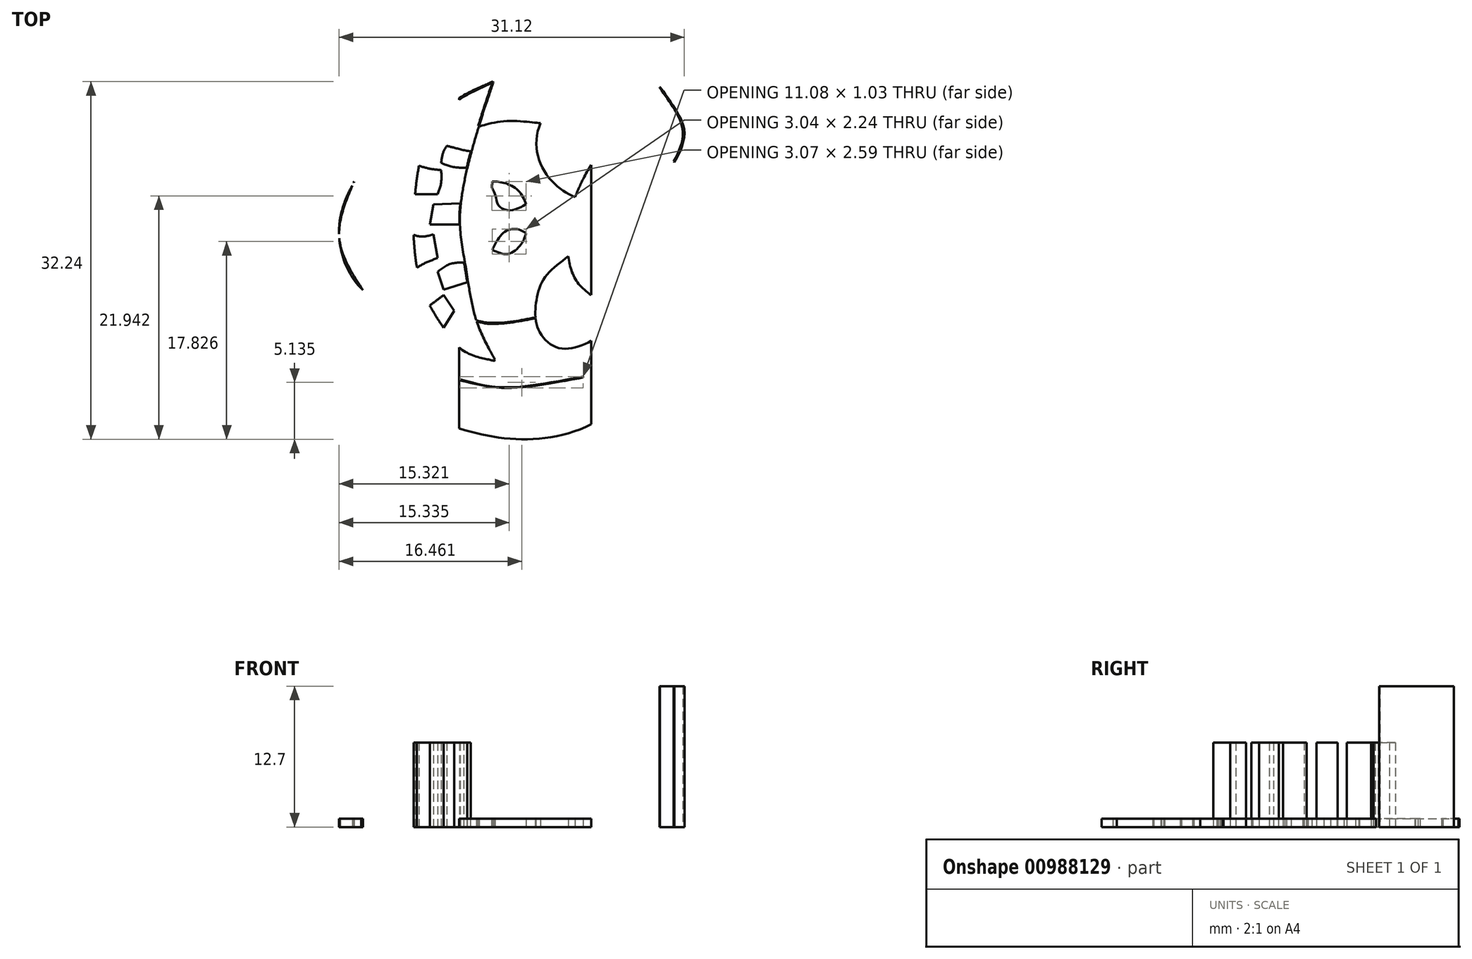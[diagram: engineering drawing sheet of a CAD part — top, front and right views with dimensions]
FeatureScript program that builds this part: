
annotation { "Feature Type Name" : "Feature", "Feature Type Description" : "" }
export const myFeature = defineFeature(function(context is Context, id is Id, definition is map)
    precondition{}
    {
        {
            var Q0;
            Q0=qCreatedBy(makeId("Top.planeOp"),FACE);
            var sketch = newSketch(context, id + "F0", { "sketchPlane" : qUnion([Q0])});
            skFitSpline(sketch, "E0", {"points": [v(-39.33, 53.9) * mm, v(-39.3, 55.65) * mm, v(-38.81, 56.88) * mm, v(-37.76, 58.43) * mm, v(-36.04, 59.76) * mm, v(-33.87, 60.77) * mm, v(-30.29, 61.56) * mm, v(-22.32, 61.02) * mm, v(-16.44, 57.51) * mm, v(-15.07, 52.72) * mm], "startDerivative": vector(-4.95, 22.44) * mm, "endDerivative": vector(4.37, -37.58) * mm});
            skFitSpline(sketch, "E1", {"points": [v(-15.07, 52.72) * mm, v(-13.86, 50.97) * mm, v(-12.98, 48.75) * mm, v(-13.85, 46.01) * mm], "startDerivative": vector(3.9, -5.4) * mm, "endDerivative": vector(-4.23, -7.42) * mm});
            skFitSpline(sketch, "E2", {"points": [v(-35.99, 54.58) * mm, v(-39.33, 53.9) * mm, v(-42.96, 50.45) * mm, v(-43.02, 47.15) * mm, v(-42.62, 44.27) * mm], "startDerivative": vector(-13.39, 1.37) * mm, "endDerivative": vector(3.7, -13.44) * mm});
            skFitSpline(sketch, "E3", {"points": [v(-39.96, 46.71) * mm, v(-42.62, 44.27) * mm, v(-43.95, 39.17) * mm, v(-41.83, 34.5) * mm, v(-38.06, 32.62) * mm], "startDerivative": vector(-12.7, -9.2) * mm, "endDerivative": vector(16.83, -5.57) * mm});
            skFitSpline(sketch, "E4", {"points": [v(-41.83, 34.5) * mm, v(-42.62, 32.56) * mm, v(-41.12, 28.84) * mm, v(-37.17, 25.72) * mm], "startDerivative": vector(-4.3, -6.86) * mm, "endDerivative": vector(11.03, -7.12) * mm});
            skFitSpline(sketch, "E5", {"points": [v(-38.62, 26.65) * mm, v(-38.4, 24.69) * mm, v(-33.93, 22.27) * mm, v(-27.64, 21.04) * mm, v(-21.05, 22.48) * mm, v(-16.17, 26.13) * mm, v(-15.07, 27.44) * mm, v(-14.53, 30.03) * mm], "startDerivative": vector(-3.87, -20.06) * mm, "endDerivative": vector(-7.64, 24.65) * mm});
            skFitSpline(sketch, "E6", {"points": [v(-19.88, 54.85) * mm, v(-17.7, 54.2) * mm, v(-15.07, 52.72) * mm], "startDerivative": vector(4.65, -1.07) * mm, "endDerivative": vector(4.98, -3.14) * mm});
            skFitSpline(sketch, "E7", {"points": [v(-33.22, 54.9) * mm, v(-27.82, 55.84) * mm, v(-22.66, 55.1) * mm], "startDerivative": vector(10.73, 2.71) * mm, "endDerivative": vector(10.4, -2.34) * mm});
            skFitSpline(sketch, "E8", {"points": [v(-16.1, 47.7) * mm, v(-13.85, 46.01) * mm, v(-12.23, 40.7) * mm, v(-14.4, 36.61) * mm, v(-16.63, 34.68) * mm], "startDerivative": vector(12.14, -5.68) * mm, "endDerivative": vector(-9.97, -7.78) * mm});
            skFitSpline(sketch, "E9", {"points": [v(-19.55, 27.44) * mm, v(-16.08, 29.12) * mm, v(-14.53, 30.03) * mm, v(-13, 33.5) * mm, v(-13.94, 37.12) * mm], "startDerivative": vector(14.06, 7.1) * mm, "endDerivative": vector(-7.18, 12.36) * mm});
            skFitSpline(sketch, "E10", {"points": [v(-13.54, 36.36) * mm, v(-12.33, 36.37) * mm, v(-8.7, 39.02) * mm, v(-7.42, 41.88) * mm, v(-7.4, 45.45) * mm, v(-8.5, 47.8) * mm, v(-9.45, 49.69) * mm, v(-9.37, 51.2) * mm, v(-9.03, 51.67) * mm, v(-8.36, 51.6) * mm, v(-8.53, 52.66) * mm, v(-9.37, 53.43) * mm, v(-10.12, 53.75) * mm, v(-10.81, 53.13) * mm, v(-11.23, 51.87) * mm, v(-10.59, 49.69) * mm, v(-10.5, 47.55) * mm, v(-11.68, 44.98) * mm, v(-12.4, 44.5) * mm, v(-13.1, 44.77) * mm], "startDerivative": vector(23.37, -4.73) * mm, "endDerivative": vector(-22.8, 5.66) * mm});
            skFitSpline(sketch, "E11", {"points": [v(-33.05, 26.34) * mm, v(-30.37, 25.77) * mm, v(-27.8, 25.7) * mm, v(-24.12, 26.22) * mm, v(-21.97, 26.62) * mm], "startDerivative": vector(11, -2.7) * mm, "endDerivative": vector(8.86, 1.67) * mm});
            skFitSpline(sketch, "E12", {"points": [v(-18.47, 48.14) * mm, v(-19.94, 49.85) * mm, v(-22.3, 51.1) * mm, v(-24.87, 50.74) * mm, v(-26.13, 48.44) * mm, v(-25.8, 45.87) * mm, v(-24.3, 43.84) * mm, v(-22.71, 42.87) * mm], "startDerivative": vector(-9.65, 13) * mm, "endDerivative": vector(12.95, -6.46) * mm});
            skFitSpline(sketch, "E13", {"points": [v(-23.3, 37.54) * mm, v(-22.32, 34.98) * mm, v(-19.16, 33.05) * mm], "startDerivative": vector(0.74, -6.31) * mm, "endDerivative": vector(7.38, -2.76) * mm});
            skFitSpline(sketch, "E14", {"points": [v(-19.16, 33.05) * mm, v(-19.6, 31.41) * mm, v(-21.62, 29.72) * mm, v(-24.3, 29.31) * mm, v(-26.01, 30.94) * mm, v(-26.25, 33.05) * mm, v(-25.57, 35.4) * mm, v(-23.3, 37.54) * mm], "startDerivative": vector(-1.66, -13.93) * mm, "endDerivative": vector(16.3, 12.24) * mm});
            skFitSpline(sketch, "E15", {"points": [v(-30.15, 38.12) * mm, v(-28.76, 37.75) * mm, v(-27.56, 38.62) * mm, v(-27.11, 39.62) * mm], "startDerivative": vector(4.14, -1.94) * mm, "endDerivative": vector(1.04, 3.31) * mm});
            skFitSpline(sketch, "E16", {"points": [v(-27.11, 39.62) * mm, v(-28, 40) * mm, v(-29.2, 39.62) * mm, v(-30.15, 38.12) * mm], "startDerivative": vector(-2.92, 1.76) * mm, "endDerivative": vector(-2.2, -4.45) * mm});
            skFitSpline(sketch, "E17", {"points": [v(-30.15, 44.28) * mm, v(-30.15, 43.62) * mm, v(-29.91, 43.16) * mm, v(-29.61, 42.14) * mm, v(-28.55, 41.68) * mm, v(-27.11, 42.23) * mm], "startDerivative": vector(-0.6, -4.34) * mm, "endDerivative": vector(5.6, 3.12) * mm});
            skFitSpline(sketch, "E18", {"points": [v(-27.11, 42.23) * mm, v(-27.8, 43.44) * mm, v(-29.14, 44.17) * mm, v(-30.15, 44.28) * mm], "startDerivative": vector(-1.53, 3.82) * mm, "endDerivative": vector(-3.36, 0.08) * mm});
            skFitSpline(sketch, "E19", {"points": [v(-30, 28.19) * mm, v(-31.65, 31.78) * mm, v(-32.6, 36.37) * mm, v(-33.12, 41.13) * mm, v(-32, 47.3) * mm, v(-30.15, 53.2) * mm], "startDerivative": vector(-10.57, 19.5) * mm, "endDerivative": vector(8.94, 26.24) * mm});
            skFitSpline(sketch, "E20", {"points": [v(-30.15, 53.2) * mm, v(-34.92, 50.14) * mm, v(-37.07, 43.64) * mm, v(-36.79, 35.77) * mm, v(-34.79, 31.44) * mm, v(-32.56, 29.09) * mm, v(-30, 28.19) * mm], "startDerivative": vector(-29.73, -13.8) * mm, "endDerivative": vector(21.62, -5.1) * mm});
            skFitSpline(sketch, "E21", {"points": [v(-32.1, 47) * mm, v(-33.52, 47.3) * mm, v(-34.27, 47.5) * mm], "startDerivative": vector(-2.65, 0.19) * mm, "endDerivative": vector(-1.62, 0.48) * mm});
            skFitSpline(sketch, "E22", {"points": [v(-34.27, 47.5) * mm, v(-34.57, 46.95) * mm, v(-34.77, 45.96) * mm], "startDerivative": vector(-0.75, -1.12) * mm, "endDerivative": vector(-0.27, -1.92) * mm});
            skFitSpline(sketch, "E23", {"points": [v(-34.77, 45.96) * mm, v(-34.04, 45.68) * mm, v(-33.1, 45.52) * mm, v(-32.47, 45.53) * mm], "startDerivative": vector(2.06, -0.9) * mm, "endDerivative": vector(1.93, 0.12) * mm});
            skFitSpline(sketch, "E24", {"points": [v(-36.77, 45.7) * mm, v(-35.85, 45.44) * mm, v(-34.77, 45.3) * mm], "startDerivative": vector(2.13, -0.61) * mm, "endDerivative": vector(2.17, -0.22) * mm});
            skFitSpline(sketch, "E25", {"points": [v(-34.77, 45.3) * mm, v(-34.77, 44.2) * mm, v(-35.1, 43.13) * mm], "startDerivative": vector(0.16, -2.22) * mm, "endDerivative": vector(-0.8, -2.13) * mm});
            skFitSpline(sketch, "E26", {"points": [v(-35.1, 43.13) * mm, v(-36.1, 43.13) * mm, v(-37.12, 43.13) * mm], "startDerivative": vector(-2.06, 0) * mm, "endDerivative": vector(-2.4, 0) * mm});
            skFitSpline(sketch, "E27", {"points": [v(-33.04, 42.3) * mm, v(-35.47, 42.22) * mm], "startDerivative": vector(-2.44, -0.09) * mm, "endDerivative": vector(-2.44, -0.09) * mm});
            skFitSpline(sketch, "E28", {"points": [v(-35.47, 42.22) * mm, v(-35.79, 40.39) * mm], "startDerivative": vector(-0.32, -1.83) * mm, "endDerivative": vector(-0.32, -1.83) * mm});
            skFitSpline(sketch, "E29", {"points": [v(-35.79, 40.39) * mm, v(-33.12, 40.39) * mm], "startDerivative": vector(2.63, 0) * mm, "endDerivative": vector(2.63, 0) * mm});
            skFitSpline(sketch, "E30", {"points": [v(-37.25, 39.46) * mm, v(-36.5, 39.3) * mm, v(-35.47, 39.5) * mm], "startDerivative": vector(2.1, -0.63) * mm, "endDerivative": vector(2.75, 0.75) * mm});
            skFitSpline(sketch, "E31", {"points": [v(-35.47, 39.5) * mm, v(-35.1, 37.37) * mm], "startDerivative": vector(0.38, -2.13) * mm, "endDerivative": vector(0.38, -2.13) * mm});
            skFitSpline(sketch, "E32", {"points": [v(-35.1, 37.37) * mm, v(-36.15, 36.96) * mm, v(-36.95, 36.51) * mm], "startDerivative": vector(-2.1, -0.75) * mm, "endDerivative": vector(-1.64, -0.98) * mm});
            skFitSpline(sketch, "E33", {"points": [v(-32.71, 37) * mm, v(-34.04, 36.82) * mm, v(-35.1, 36.13) * mm], "startDerivative": vector(-2.66, -0.07) * mm, "endDerivative": vector(-2.01, -1.63) * mm});
            skFitSpline(sketch, "E34", {"points": [v(-35.1, 36.13) * mm, v(-34.55, 34.52) * mm], "startDerivative": vector(0.54, -1.6) * mm, "endDerivative": vector(0.54, -1.6) * mm});
            skFitSpline(sketch, "E35", {"points": [v(-34.55, 34.52) * mm, v(-32.41, 35.2) * mm], "startDerivative": vector(2.1, 0.68) * mm, "endDerivative": vector(2.1, 0.68) * mm});
            skFitSpline(sketch, "E36", {"points": [v(-35.79, 33.1) * mm, v(-34.55, 34.04) * mm], "startDerivative": vector(1.24, 0.9) * mm, "endDerivative": vector(1.24, 0.9) * mm});
            skFitSpline(sketch, "E37", {"points": [v(-34.55, 34.04) * mm, v(-33.6, 32.62) * mm], "startDerivative": vector(0.95, -1.42) * mm, "endDerivative": vector(0.95, -1.42) * mm});
            skFitSpline(sketch, "E38", {"points": [v(-33.6, 32.62) * mm, v(-34.55, 31.1) * mm], "startDerivative": vector(-0.95, -1.52) * mm, "endDerivative": vector(-0.95, -1.52) * mm});
            skFitSpline(sketch, "E39", {"points": [v(-31.43, 49.3) * mm, v(-29, 49.76) * mm, v(-25.77, 49.61) * mm], "startDerivative": vector(5, 1.26) * mm, "endDerivative": vector(6.26, -0.6) * mm});
            skFitSpline(sketch, "E40", {"points": [v(-31.65, 31.78) * mm, v(-30.53, 31.55) * mm, v(-28.49, 31.64) * mm, v(-26.27, 32.02) * mm], "startDerivative": vector(3.97, -1.1) * mm, "endDerivative": vector(5.9, 1.12) * mm});
            skFitSpline(sketch, "E41", {"points": [v(-13.85, 46.01) * mm, v(-13.38, 45.62) * mm, v(-13.1, 44.77) * mm], "startDerivative": vector(0.96, -1.11) * mm, "endDerivative": vector(0.12, -1.6) * mm});
            skFitSpline(sketch, "E42", {"points": [v(-13.54, 36.36) * mm, v(-13, 33.5) * mm, v(-14.53, 30.03) * mm], "startDerivative": vector(2.2, -6) * mm, "endDerivative": vector(-6.3, -4.5) * mm});
            skFitSpline(sketch, "E43", {"points": [v(-18.47, 48.14) * mm, v(-20.62, 46.55) * mm, v(-22.2, 44.02) * mm, v(-22.71, 42.87) * mm], "startDerivative": vector(-6.1, -3.67) * mm, "endDerivative": vector(-1.87, -4.03) * mm});
            skFitSpline(sketch, "E44", {"points": [v(-42.62, 44.27) * mm, v(-43.95, 39.17) * mm, v(-41.83, 34.5) * mm], "startDerivative": vector(-4.46, -10.28) * mm, "endDerivative": vector(6, -9.2) * mm});
            skLineSegment(sketch, "E45.left", {"start": v(-21.23, 60.69) * mm, "end": v(-21.23, 50.72) * mm});
            skLineSegment(sketch, "E45.right", {"start": v(-33.16, 60.92) * mm, "end": v(-33.16, 51.65) * mm});
            skFitSpline(sketch, "E46.0", {"points": [v(-39.58, 26.84) * mm, v(-39.63, 26.61) * mm, v(-39.7, 26.11) * mm, v(-39.7, 25.38) * mm, v(-39.54, 24.75) * mm, v(-39.36, 24.36) * mm, v(-39.16, 24.06) * mm, v(-38.94, 23.79) * mm, v(-38.64, 23.48) * mm, v(-38.22, 23.15) * mm, v(-37.61, 22.75) * mm, v(-36.77, 22.31) * mm, v(-35.67, 21.85) * mm, v(-34.53, 21.43) * mm, v(-33.4, 21.06) * mm, v(-31.88, 20.63) * mm, v(-29.97, 20.22) * mm, v(-27.63, 20) * mm, v(-25.61, 20.1) * mm, v(-23.99, 20.38) * mm, v(-22.77, 20.7) * mm, v(-21.77, 21.06) * mm, v(-20.97, 21.42) * mm, v(-20.19, 21.82) * mm, v(-19.24, 22.38) * mm, v(-18.19, 23.12) * mm, v(-17.23, 23.88) * mm, v(-16.39, 24.6) * mm, v(-15.8, 25.13) * mm, v(-15.42, 25.49) * mm, v(-15.17, 25.73) * mm, v(-14.95, 25.97) * mm, v(-14.73, 26.2) * mm, v(-14.53, 26.47) * mm, v(-14.34, 26.74) * mm, v(-14.17, 27.04) * mm, v(-13.98, 27.38) * mm, v(-13.8, 27.77) * mm, v(-13.59, 28.35) * mm, v(-13.4, 29.18) * mm, v(-13.48, 29.94) * mm, v(-13.6, 30.32) * mm]});
            skFitSpline(sketch, "E47.0", {"points": [v(-42.9, 35.18) * mm, v(-43, 35.04) * mm, v(-43.19, 34.74) * mm, v(-43.5, 34.19) * mm, v(-43.72, 33.62) * mm, v(-43.84, 33.1) * mm, v(-43.9, 32.68) * mm, v(-43.9, 32.25) * mm, v(-43.84, 31.68) * mm, v(-43.7, 30.98) * mm, v(-43.4, 30.15) * mm, v(-43, 29.34) * mm, v(-42.51, 28.55) * mm, v(-41.94, 27.81) * mm, v(-41.3, 27.16) * mm, v(-40.42, 26.37) * mm, v(-39.25, 25.54) * mm, v(-38.32, 24.94) * mm, v(-37.86, 24.65) * mm]});
            skFitSpline(sketch, "E48.0", {"points": [v(-43.78, 44.77) * mm, v(-43.97, 44.34) * mm, v(-44.35, 43.46) * mm, v(-44.77, 42.31) * mm, v(-45.03, 41.36) * mm, v(-45.17, 40.63) * mm, v(-45.25, 39.87) * mm, v(-45.24, 39.23) * mm, v(-45.18, 38.71) * mm, v(-45.1, 38.21) * mm, v(-44.93, 37.6) * mm, v(-44.67, 36.9) * mm, v(-44.26, 36.02) * mm, v(-43.66, 34.98) * mm, v(-43.14, 34.2) * mm, v(-42.9, 33.81) * mm]});
            skFitSpline(sketch, "E49.0", {"points": [v(-35.86, 55.85) * mm, v(-36.54, 55.92) * mm, v(-37.93, 55.86) * mm, v(-39.67, 55.2) * mm, v(-41.1, 54.36) * mm, v(-42.12, 53.58) * mm, v(-42.9, 52.83) * mm, v(-43.45, 52.16) * mm, v(-43.8, 51.62) * mm, v(-44.06, 51.14) * mm, v(-44.22, 50.73) * mm, v(-44.34, 50.33) * mm, v(-44.44, 49.83) * mm, v(-44.5, 49.06) * mm, v(-44.47, 48.36) * mm, v(-44.39, 47.74) * mm, v(-44.34, 47.38) * mm, v(-44.3, 47.11) * mm, v(-44.27, 46.86) * mm, v(-44.24, 46.55) * mm, v(-44.2, 46.16) * mm, v(-44.15, 45.62) * mm, v(-44.06, 44.9) * mm, v(-43.93, 44.26) * mm, v(-43.84, 43.93) * mm]});
            skFitSpline(sketch, "E50.0", {"points": [v(-40.58, 53.62) * mm, v(-40.65, 53.95) * mm, v(-40.71, 54.6) * mm, v(-40.65, 55.49) * mm, v(-40.47, 56.28) * mm, v(-40.24, 56.86) * mm, v(-40.04, 57.29) * mm, v(-39.88, 57.6) * mm, v(-39.7, 57.92) * mm, v(-39.41, 58.37) * mm, v(-39.08, 58.84) * mm, v(-38.68, 59.3) * mm, v(-38.25, 59.75) * mm, v(-37.67, 60.23) * mm, v(-36.94, 60.72) * mm, v(-36.2, 61.14) * mm, v(-35.42, 61.52) * mm, v(-34.6, 61.86) * mm, v(-33.74, 62.16) * mm, v(-32.8, 62.43) * mm, v(-31.73, 62.65) * mm, v(-30.54, 62.82) * mm, v(-29.2, 62.93) * mm, v(-27.72, 62.96) * mm, v(-26.15, 62.9) * mm, v(-24.54, 62.75) * mm, v(-22.91, 62.48) * mm, v(-21.3, 62.08) * mm, v(-19.78, 61.53) * mm, v(-18.36, 60.84) * mm, v(-17.08, 60) * mm, v(-16.16, 59.18) * mm, v(-15.53, 58.43) * mm, v(-14.99, 57.63) * mm, v(-14.5, 56.58) * mm, v(-14.15, 55.3) * mm, v(-13.94, 54.06) * mm, v(-13.85, 53.26) * mm, v(-13.8, 52.86) * mm]});
            skFitSpline(sketch, "E51", {"points": [v(-13.8, 52.86) * mm, v(-13.4, 52.11) * mm, v(-12.4, 52.26) * mm, v(-11.8, 53.48) * mm, v(-10.42, 54.64) * mm, v(-7.7, 53.31) * mm, v(-7.3, 50.67) * mm, v(-8.48, 50.2) * mm, v(-7.27, 47.84) * mm, v(-6.18, 44.23) * mm, v(-6.84, 39.73) * mm, v(-9.92, 36.36) * mm, v(-12.45, 35.23) * mm], "startDerivative": vector(5.04, -18.54) * mm, "endDerivative": vector(-27.24, -9.28) * mm});
            skFitSpline(sketch, "E52.0", {"points": [v(-12.4, 36.77) * mm, v(-12.3, 36.5) * mm, v(-12.12, 35.97) * mm, v(-11.9, 35.12) * mm, v(-11.78, 34.2) * mm, v(-11.78, 33.21) * mm, v(-11.91, 32.14) * mm, v(-12.24, 31.03) * mm, v(-12.83, 29.94) * mm, v(-13.46, 29.31) * mm, v(-13.83, 29.05) * mm]});
            skFitSpline(sketch, "E53", {"points": [v(-38.62, 26.65) * mm, v(-41.12, 28.84) * mm, v(-42.62, 32.56) * mm, v(-41.83, 34.5) * mm], "startDerivative": vector(-7.97, 4.63) * mm, "endDerivative": vector(4.08, 6.27) * mm});
            skFitSpline(sketch, "E54.0", {"points": [v(-33.24, 54.97) * mm, v(-32.35, 55.2) * mm, v(-30.56, 55.65) * mm, v(-27.88, 56.02) * mm, v(-25.25, 55.75) * mm, v(-23.51, 55.36) * mm, v(-22.64, 55.17) * mm]});
            skLineSegment(sketch, "E55", {"start": v(-22.64, 55.17) * mm, "end": v(-22.66, 55.1) * mm});
            skLineSegment(sketch, "E56", {"start": v(-33.24, 54.97) * mm, "end": v(-33.22, 54.9) * mm});
            skFitSpline(sketch, "E57.0", {"points": [v(-39.26, 53.91) * mm, v(-39.31, 54.14) * mm, v(-39.36, 54.6) * mm, v(-39.32, 55.17) * mm, v(-39.24, 55.6) * mm, v(-39.14, 55.98) * mm, v(-38.97, 56.4) * mm, v(-38.7, 56.94) * mm, v(-38.36, 57.53) * mm, v(-37.94, 58.12) * mm, v(-37.44, 58.67) * mm, v(-36.87, 59.14) * mm, v(-36.23, 59.57) * mm, v(-35.57, 59.95) * mm, v(-34.87, 60.3) * mm, v(-34.13, 60.6) * mm, v(-33.34, 60.88) * mm, v(-32.47, 61.12) * mm, v(-31.5, 61.33) * mm, v(-30.4, 61.48) * mm, v(-29.13, 61.58) * mm, v(-27.72, 61.61) * mm, v(-26.24, 61.56) * mm, v(-24.71, 61.42) * mm, v(-23.18, 61.16) * mm, v(-21.7, 60.78) * mm, v(-20.3, 60.28) * mm, v(-19.02, 59.66) * mm, v(-17.9, 58.93) * mm, v(-16.96, 58.09) * mm, v(-16.25, 57.15) * mm, v(-15.78, 56.12) * mm, v(-15.37, 54.66) * mm, v(-15.23, 53.5) * mm, v(-15.14, 52.7) * mm]});
            skFitSpline(sketch, "E58.0", {"points": [v(-36, 54.5) * mm, v(-36.55, 54.56) * mm, v(-37.36, 54.53) * mm, v(-38.5, 54.2) * mm, v(-39.4, 53.8) * mm, v(-40.34, 53.24) * mm, v(-41.25, 52.55) * mm, v(-42.05, 51.77) * mm, v(-42.57, 51.07) * mm, v(-42.87, 50.5) * mm, v(-43.07, 49.93) * mm, v(-43.16, 49.2) * mm, v(-43.12, 48.34) * mm, v(-43.01, 47.64) * mm, v(-42.94, 47.08) * mm, v(-42.88, 46.54) * mm, v(-42.82, 45.89) * mm, v(-42.73, 45.1) * mm, v(-42.62, 44.56) * mm, v(-42.54, 44.29) * mm]});
            skLineSegment(sketch, "E59", {"start": v(-35.99, 54.58) * mm, "end": v(-36.02, 54.51) * mm});
            skLineSegment(sketch, "E60", {"start": v(-39.3, 53.83) * mm, "end": v(-39.33, 53.9) * mm});
            skFitSpline(sketch, "E61.0", {"points": [v(-39.35, 53.91) * mm, v(-39.73, 53.48) * mm, v(-40.62, 52.72) * mm, v(-41.76, 51.86) * mm, v(-42.51, 51.16) * mm, v(-42.95, 50.6) * mm, v(-43.2, 49.98) * mm, v(-43.28, 49.33) * mm, v(-43.26, 48.65) * mm, v(-43.17, 47.97) * mm, v(-43.07, 47.3) * mm, v(-43, 46.68) * mm, v(-42.94, 46.07) * mm, v(-42.86, 45.28) * mm, v(-42.76, 44.68) * mm, v(-42.64, 44.26) * mm]});
            skLineSegment(sketch, "E62", {"start": v(-39.26, 53.93) * mm, "end": v(-39.26, 53.93) * mm});
            skLineSegment(sketch, "E63", {"start": v(-39.33, 53.9) * mm, "end": v(-39.26, 53.93) * mm});
            skFitSpline(sketch, "E64.0", {"points": [v(-39.41, 53.96) * mm, v(-39.78, 53.54) * mm, v(-40.66, 52.78) * mm, v(-41.81, 51.92) * mm, v(-42.57, 51.21) * mm, v(-43.01, 50.64) * mm, v(-43.27, 50) * mm, v(-43.36, 49.33) * mm, v(-43.34, 48.64) * mm, v(-43.25, 47.96) * mm, v(-43.14, 47.3) * mm, v(-43.07, 46.67) * mm, v(-43.01, 46.06) * mm, v(-42.93, 45.27) * mm, v(-42.83, 44.67) * mm, v(-42.71, 44.24) * mm]});
            skLineSegment(sketch, "E65", {"start": v(-39.36, 53.9) * mm, "end": v(-39.33, 53.9) * mm});
            skLineSegment(sketch, "E66", {"start": v(-39.42, 53.95) * mm, "end": v(-39.35, 53.95) * mm});
            skFitSpline(sketch, "E67.0", {"points": [v(-39.92, 46.65) * mm, v(-40.18, 46.46) * mm, v(-40.72, 46.08) * mm, v(-41.49, 45.46) * mm, v(-42.08, 44.86) * mm, v(-42.51, 44.3) * mm, v(-42.91, 43.67) * mm, v(-43.34, 42.77) * mm, v(-43.83, 41.18) * mm, v(-44.01, 39) * mm, v(-43.33, 36.53) * mm, v(-42.2, 34.86) * mm, v(-41.05, 33.95) * mm, v(-39.78, 33.27) * mm, v(-38.73, 32.92) * mm, v(-38.03, 32.7) * mm]});
            skLineSegment(sketch, "E68", {"start": v(-39.96, 46.71) * mm, "end": v(-39.92, 46.65) * mm});
            skLineSegment(sketch, "E69", {"start": v(-42.62, 44.27) * mm, "end": v(-42.55, 44.22) * mm});
            skFitSpline(sketch, "E70.0", {"points": [v(-42.55, 44.24) * mm, v(-42.92, 43.38) * mm, v(-43.47, 42.1) * mm, v(-43.87, 40.42) * mm, v(-43.93, 39.2) * mm, v(-43.68, 38.02) * mm, v(-43.01, 36.46) * mm, v(-42.27, 35.31) * mm, v(-41.77, 34.55) * mm]});
            skLineSegment(sketch, "E71", {"start": v(-42.71, 44.24) * mm, "end": v(-42.65, 44.19) * mm});
            skLineSegment(sketch, "E72", {"start": v(-42.64, 44.26) * mm, "end": v(-42.62, 44.27) * mm});
            skLineSegment(sketch, "E73", {"start": v(-38.03, 32.7) * mm, "end": v(-38.06, 32.62) * mm});
            skFitSpline(sketch, "E74.trimOffspring", {"points": [v(-39.92, 46.65) * mm, v(-40.18, 46.46) * mm, v(-40.72, 46.08) * mm, v(-41.49, 45.46) * mm, v(-42.08, 44.86) * mm, v(-42.51, 44.3) * mm, v(-42.91, 43.67) * mm, v(-43.34, 42.77) * mm, v(-43.83, 41.18) * mm, v(-44.01, 39) * mm, v(-43.33, 36.53) * mm, v(-42.2, 34.86) * mm, v(-41.05, 33.95) * mm, v(-39.78, 33.27) * mm, v(-38.73, 32.92) * mm, v(-38.03, 32.7) * mm]});
            skFitSpline(sketch, "E75.0", {"points": [v(-38.66, 26.59) * mm, v(-39, 26.78) * mm, v(-39.64, 27.2) * mm, v(-40.4, 27.86) * mm, v(-40.97, 28.5) * mm, v(-41.38, 29.05) * mm, v(-41.76, 29.66) * mm, v(-42.21, 30.51) * mm, v(-42.55, 31.4) * mm, v(-42.7, 32.22) * mm, v(-42.7, 32.79) * mm, v(-42.58, 33.29) * mm, v(-42.33, 33.9) * mm, v(-42.06, 34.29) * mm, v(-41.9, 34.55) * mm]});
            skLineSegment(sketch, "E76", {"start": v(-41.9, 34.55) * mm, "end": v(-41.84, 34.53) * mm});
            skLineSegment(sketch, "E77", {"start": v(-41.77, 34.56) * mm, "end": v(-41.83, 34.5) * mm});
            skFitSpline(sketch, "E78.0", {"points": [v(-41.76, 34.47) * mm, v(-41.94, 34.18) * mm, v(-42.22, 33.75) * mm, v(-42.46, 33.13) * mm, v(-42.56, 32.6) * mm, v(-42.53, 32.01) * mm, v(-42.35, 31.14) * mm, v(-41.95, 30.21) * mm, v(-41.4, 29.32) * mm, v(-40.76, 28.5) * mm, v(-39.8, 27.6) * mm, v(-38.5, 26.66) * mm, v(-37.59, 26.08) * mm, v(-37.13, 25.78) * mm]});
            skLineSegment(sketch, "E79", {"start": v(-38.62, 26.67) * mm, "end": v(-38.58, 26.73) * mm});
            skLineSegment(sketch, "E80", {"start": v(-37.17, 25.72) * mm, "end": v(-37.13, 25.78) * mm});
            skFitSpline(sketch, "E81.0", {"points": [v(-38.7, 26.67) * mm, v(-38.73, 26.46) * mm, v(-38.8, 26.03) * mm, v(-38.8, 25.38) * mm, v(-38.58, 24.74) * mm, v(-38.07, 24.15) * mm, v(-37.32, 23.62) * mm, v(-36.4, 23.13) * mm, v(-35.35, 22.69) * mm, v(-34.24, 22.29) * mm, v(-33.13, 21.93) * mm, v(-31.66, 21.5) * mm, v(-29.83, 21.12) * mm, v(-27.6, 20.91) * mm, v(-25.32, 21.02) * mm, v(-23.41, 21.43) * mm, v(-21.91, 21.97) * mm, v(-20.81, 22.5) * mm, v(-19.74, 23.14) * mm, v(-18.73, 23.85) * mm, v(-17.8, 24.58) * mm, v(-16.98, 25.27) * mm, v(-16.42, 25.79) * mm, v(-16.05, 26.14) * mm, v(-15.73, 26.45) * mm, v(-15.48, 26.72) * mm, v(-15.26, 27) * mm, v(-15.1, 27.23) * mm, v(-14.95, 27.49) * mm, v(-14.73, 27.89) * mm, v(-14.49, 28.47) * mm, v(-14.32, 29.25) * mm, v(-14.37, 29.79) * mm, v(-14.46, 30.05) * mm]});
            skFitSpline(sketch, "E82.0", {"points": [v(-13.47, 36.38) * mm, v(-13.29, 35.88) * mm, v(-13.06, 35.16) * mm, v(-12.91, 34.12) * mm, v(-12.9, 33.28) * mm, v(-13.03, 32.37) * mm, v(-13.4, 31.16) * mm, v(-13.95, 30.36) * mm, v(-14.49, 29.97) * mm]});
            skFitSpline(sketch, "E83.0", {"points": [v(-33.03, 26.42) * mm, v(-32.12, 26.2) * mm, v(-30.74, 25.86) * mm, v(-29.3, 25.73) * mm, v(-28.4, 25.73) * mm, v(-27.68, 25.78) * mm, v(-26.89, 25.86) * mm, v(-26.06, 25.98) * mm, v(-25.24, 26.1) * mm, v(-24.45, 26.24) * mm, v(-23.74, 26.36) * mm, v(-22.9, 26.52) * mm, v(-22.35, 26.62) * mm, v(-21.98, 26.7) * mm]});
            skLineSegment(sketch, "E84", {"start": v(-21.98, 26.7) * mm, "end": v(-21.97, 26.62) * mm});
            skLineSegment(sketch, "E85", {"start": v(-33.03, 26.42) * mm, "end": v(-33.05, 26.34) * mm});
            skFitSpline(sketch, "E86.0", {"points": [v(-19.59, 27.5) * mm, v(-19.3, 27.66) * mm, v(-18.7, 27.95) * mm, v(-17.86, 28.38) * mm, v(-17.06, 28.76) * mm, v(-16.46, 29.04) * mm, v(-16.03, 29.23) * mm, v(-15.64, 29.4) * mm, v(-15.2, 29.58) * mm, v(-14.83, 29.84) * mm, v(-14.52, 30.15) * mm, v(-14.2, 30.53) * mm, v(-13.83, 31.12) * mm, v(-13.44, 31.97) * mm, v(-13.15, 32.88) * mm, v(-13.02, 33.8) * mm, v(-13.07, 34.66) * mm, v(-13.33, 35.78) * mm, v(-13.7, 36.57) * mm, v(-14, 37.08) * mm]});
            skLineSegment(sketch, "E87", {"start": v(-19.59, 27.5) * mm, "end": v(-19.55, 27.44) * mm});
            skLineSegment(sketch, "E88", {"start": v(-14.59, 30.08) * mm, "end": v(-14.53, 30.03) * mm});
            skFitSpline(sketch, "E89.0", {"points": [v(-13.56, 36.28) * mm, v(-13.44, 36.26) * mm, v(-13.2, 36.2) * mm, v(-12.77, 36.18) * mm, v(-12.27, 36.29) * mm, v(-11.64, 36.57) * mm, v(-10.95, 36.98) * mm, v(-10.23, 37.5) * mm, v(-9.52, 38.07) * mm, v(-8.89, 38.69) * mm, v(-8.37, 39.3) * mm, v(-7.85, 40.09) * mm, v(-7.54, 40.9) * mm, v(-7.35, 41.77) * mm, v(-7.24, 42.48) * mm, v(-7.17, 43.22) * mm, v(-7.15, 43.97) * mm, v(-7.18, 44.7) * mm, v(-7.32, 45.65) * mm, v(-7.7, 46.65) * mm, v(-8.33, 47.68) * mm, v(-8.98, 48.66) * mm, v(-9.35, 49.46) * mm, v(-9.44, 50.11) * mm, v(-9.42, 50.6) * mm, v(-9.36, 50.96) * mm, v(-9.3, 51.22) * mm, v(-9.24, 51.39) * mm, v(-9.17, 51.51) * mm, v(-9.1, 51.58) * mm, v(-9.01, 51.6) * mm, v(-8.86, 51.58) * mm, v(-8.68, 51.53) * mm, v(-8.54, 51.5) * mm, v(-8.42, 51.5) * mm, v(-8.33, 51.51) * mm, v(-8.26, 51.58) * mm, v(-8.22, 51.66) * mm, v(-8.2, 51.75) * mm, v(-8.2, 51.88) * mm, v(-8.22, 52.08) * mm, v(-8.3, 52.32) * mm, v(-8.4, 52.57) * mm, v(-8.51, 52.8) * mm, v(-8.7, 53.03) * mm, v(-8.97, 53.26) * mm, v(-9.24, 53.44) * mm, v(-9.46, 53.58) * mm, v(-9.62, 53.69) * mm, v(-9.79, 53.77) * mm, v(-9.96, 53.83) * mm, v(-10.14, 53.84) * mm, v(-10.31, 53.78) * mm, v(-10.47, 53.67) * mm, v(-10.66, 53.48) * mm, v(-10.88, 53.19) * mm, v(-11.1, 52.8) * mm, v(-11.28, 52.38) * mm, v(-11.34, 51.9) * mm, v(-11.25, 51.37) * mm, v(-11.07, 50.8) * mm, v(-10.86, 50.23) * mm, v(-10.65, 49.67) * mm, v(-10.52, 49.14) * mm, v(-10.45, 48.62) * mm, v(-10.47, 48.08) * mm, v(-10.57, 47.5) * mm, v(-10.77, 46.86) * mm, v(-11.03, 46.22) * mm, v(-11.33, 45.62) * mm, v(-11.65, 45.12) * mm, v(-11.95, 44.76) * mm, v(-12.18, 44.6) * mm, v(-12.34, 44.57) * mm, v(-12.5, 44.59) * mm, v(-12.72, 44.7) * mm, v(-12.95, 44.8) * mm, v(-13.08, 44.84) * mm]});
            skFitSpline(sketch, "E90.0", {"points": [v(-13.56, 36.28) * mm, v(-13.44, 36.26) * mm, v(-13.2, 36.2) * mm, v(-12.77, 36.18) * mm, v(-12.27, 36.29) * mm, v(-11.64, 36.57) * mm, v(-10.95, 36.98) * mm, v(-10.23, 37.5) * mm, v(-9.52, 38.07) * mm, v(-8.89, 38.69) * mm, v(-8.37, 39.3) * mm, v(-7.85, 40.09) * mm, v(-7.54, 40.9) * mm, v(-7.35, 41.77) * mm, v(-7.24, 42.48) * mm, v(-7.17, 43.22) * mm, v(-7.15, 43.97) * mm, v(-7.18, 44.7) * mm, v(-7.32, 45.65) * mm, v(-7.7, 46.65) * mm, v(-8.33, 47.68) * mm, v(-8.98, 48.66) * mm, v(-9.35, 49.46) * mm, v(-9.44, 50.11) * mm, v(-9.42, 50.6) * mm, v(-9.36, 50.96) * mm, v(-9.3, 51.22) * mm, v(-9.24, 51.39) * mm, v(-9.17, 51.51) * mm, v(-9.1, 51.58) * mm, v(-9.01, 51.6) * mm, v(-8.86, 51.58) * mm, v(-8.68, 51.53) * mm, v(-8.54, 51.5) * mm, v(-8.42, 51.5) * mm, v(-8.33, 51.51) * mm, v(-8.26, 51.58) * mm, v(-8.22, 51.66) * mm, v(-8.2, 51.75) * mm, v(-8.2, 51.88) * mm, v(-8.22, 52.08) * mm, v(-8.3, 52.32) * mm, v(-8.4, 52.57) * mm, v(-8.51, 52.8) * mm, v(-8.7, 53.03) * mm, v(-8.97, 53.26) * mm, v(-9.24, 53.44) * mm, v(-9.46, 53.58) * mm, v(-9.62, 53.69) * mm, v(-9.79, 53.77) * mm, v(-9.96, 53.83) * mm, v(-10.14, 53.84) * mm, v(-10.31, 53.78) * mm, v(-10.47, 53.67) * mm, v(-10.66, 53.48) * mm, v(-10.88, 53.19) * mm, v(-11.1, 52.8) * mm, v(-11.28, 52.38) * mm, v(-11.34, 51.9) * mm, v(-11.25, 51.37) * mm, v(-11.07, 50.8) * mm, v(-10.86, 50.23) * mm, v(-10.65, 49.67) * mm, v(-10.52, 49.14) * mm, v(-10.45, 48.62) * mm, v(-10.47, 48.08) * mm, v(-10.57, 47.5) * mm, v(-10.77, 46.86) * mm, v(-11.03, 46.22) * mm, v(-11.33, 45.62) * mm, v(-11.65, 45.12) * mm, v(-11.95, 44.76) * mm, v(-12.18, 44.6) * mm, v(-12.34, 44.57) * mm, v(-12.5, 44.59) * mm, v(-12.72, 44.7) * mm, v(-12.95, 44.8) * mm, v(-13.08, 44.84) * mm]});
            skFitSpline(sketch, "E91.0", {"points": [v(-13.79, 46.06) * mm, v(-13.72, 45.98) * mm, v(-13.59, 45.9) * mm, v(-13.4, 45.76) * mm, v(-13.27, 45.61) * mm, v(-13.17, 45.42) * mm, v(-13.07, 45.14) * mm, v(-13.03, 44.91) * mm, v(-13.02, 44.77) * mm]});
            skFitSpline(sketch, "E92.0", {"points": [v(-15, 52.76) * mm, v(-14.84, 52.54) * mm, v(-14.52, 52.08) * mm, v(-14.1, 51.5) * mm, v(-13.79, 51) * mm, v(-13.46, 50.48) * mm, v(-13.1, 49.78) * mm, v(-12.86, 48.87) * mm, v(-12.94, 47.9) * mm, v(-13.27, 46.93) * mm, v(-13.6, 46.29) * mm, v(-13.78, 45.98) * mm]});
            skLineSegment(sketch, "E93", {"start": v(-15, 52.76) * mm, "end": v(-15.07, 52.77) * mm});
            skFitSpline(sketch, "E94.0", {"points": [v(-19.52, 27.37) * mm, v(-18.93, 27.67) * mm, v(-18.06, 28.11) * mm, v(-17, 28.63) * mm, v(-16.4, 28.9) * mm, v(-15.97, 29.09) * mm, v(-15.58, 29.25) * mm, v(-15.14, 29.45) * mm, v(-14.73, 29.72) * mm, v(-14.4, 30.04) * mm, v(-14.08, 30.44) * mm, v(-13.7, 31.05) * mm, v(-13.3, 31.91) * mm, v(-13, 32.84) * mm, v(-12.87, 33.78) * mm, v(-12.92, 34.68) * mm, v(-13.19, 35.83) * mm, v(-13.57, 36.64) * mm, v(-13.87, 37.16) * mm]});
            skLineSegment(sketch, "E95", {"start": v(-13.54, 36.36) * mm, "end": v(-13.47, 36.39) * mm});
            skFitSpline(sketch, "E96.0", {"points": [v(-16.07, 47.78) * mm, v(-15.81, 47.66) * mm, v(-15.33, 47.42) * mm, v(-14.65, 46.98) * mm, v(-14.13, 46.5) * mm, v(-13.72, 45.99) * mm, v(-13.33, 45.4) * mm, v(-12.87, 44.53) * mm, v(-12.43, 43.36) * mm, v(-12.16, 42.12) * mm, v(-12.1, 40.88) * mm, v(-12.3, 39.73) * mm, v(-12.74, 38.68) * mm, v(-13.32, 37.75) * mm, v(-14, 36.92) * mm, v(-14.67, 36.22) * mm, v(-15.32, 35.63) * mm, v(-15.96, 35.1) * mm, v(-16.37, 34.78) * mm, v(-16.58, 34.62) * mm]});
            skFitSpline(sketch, "E97.trimOffspring", {"points": [v(-16.07, 47.78) * mm, v(-15.81, 47.66) * mm, v(-15.33, 47.42) * mm, v(-14.65, 46.98) * mm, v(-14.13, 46.5) * mm, v(-13.72, 45.99) * mm, v(-13.33, 45.4) * mm, v(-12.87, 44.53) * mm, v(-12.43, 43.36) * mm, v(-12.16, 42.12) * mm, v(-12.1, 40.88) * mm, v(-12.3, 39.73) * mm, v(-12.74, 38.68) * mm, v(-13.32, 37.75) * mm, v(-14, 36.92) * mm, v(-14.67, 36.22) * mm, v(-15.32, 35.63) * mm, v(-15.96, 35.1) * mm, v(-16.37, 34.78) * mm, v(-16.58, 34.62) * mm]});
            skLineSegment(sketch, "E98", {"start": v(-16.63, 34.68) * mm, "end": v(-16.58, 34.62) * mm});
            skFitSpline(sketch, "E99.0", {"points": [v(-16.13, 47.64) * mm, v(-15.88, 47.52) * mm, v(-15.4, 47.29) * mm, v(-14.75, 46.86) * mm, v(-14.24, 46.39) * mm, v(-13.85, 45.9) * mm, v(-13.46, 45.32) * mm, v(-13.01, 44.47) * mm, v(-12.58, 43.31) * mm, v(-12.3, 42.1) * mm, v(-12.25, 40.89) * mm, v(-12.45, 39.77) * mm, v(-12.88, 38.75) * mm, v(-13.45, 37.83) * mm, v(-14.1, 37.02) * mm, v(-14.77, 36.33) * mm, v(-15.42, 35.74) * mm, v(-16.05, 35.22) * mm, v(-16.47, 34.9) * mm, v(-16.68, 34.74) * mm]});
            skLineSegment(sketch, "E100", {"start": v(-13.9, 45.97) * mm, "end": v(-13.85, 46.01) * mm});
            skLineSegment(sketch, "E101", {"start": v(-16.13, 47.64) * mm, "end": v(-16.1, 47.7) * mm});
            skFitSpline(sketch, "E102.0", {"points": [v(-19.9, 54.77) * mm, v(-19.51, 54.68) * mm, v(-18.74, 54.5) * mm, v(-17.57, 54.1) * mm, v(-16.35, 53.44) * mm, v(-15.52, 52.91) * mm, v(-15.1, 52.65) * mm]});
            skLineSegment(sketch, "E103", {"start": v(-19.88, 54.85) * mm, "end": v(-19.9, 54.77) * mm});
            skLineSegment(sketch, "E104", {"start": v(-15.1, 52.65) * mm, "end": v(-15.07, 52.72) * mm});
            skFitSpline(sketch, "E105.0", {"points": [v(-31.4, 49.23) * mm, v(-31, 49.34) * mm, v(-30.16, 49.55) * mm, v(-28.84, 49.73) * mm, v(-27.35, 49.69) * mm, v(-26.3, 49.59) * mm, v(-25.78, 49.54) * mm]});
            skFitSpline(sketch, "E106.trimOffspring", {"points": [v(-30, 28.19) * mm, v(-31.65, 31.78) * mm, v(-32.6, 36.37) * mm, v(-33.12, 41.13) * mm, v(-32, 47.3) * mm, v(-30.15, 53.2) * mm], "startDerivative": vector(-10.57, 19.5) * mm, "endDerivative": vector(8.94, 26.24) * mm});
            skFitSpline(sketch, "E107.0", {"points": [v(-31.67, 31.7) * mm, v(-31.5, 31.66) * mm, v(-31.18, 31.57) * mm, v(-30.64, 31.47) * mm, v(-29.98, 31.44) * mm, v(-29.24, 31.48) * mm, v(-28.47, 31.56) * mm, v(-27.72, 31.68) * mm, v(-26.99, 31.8) * mm, v(-26.5, 31.9) * mm, v(-26.25, 31.95) * mm]});
            skLineSegment(sketch, "E108", {"start": v(-31.65, 31.78) * mm, "end": v(-31.62, 31.69) * mm});
            skFitSpline(sketch, "E109.0", {"points": [v(-30.19, 53.27) * mm, v(-30.8, 52.98) * mm, v(-32.06, 52.4) * mm, v(-33.53, 51.55) * mm, v(-34.55, 50.7) * mm, v(-35.2, 49.94) * mm, v(-35.75, 49.07) * mm, v(-36.34, 47.77) * mm, v(-36.85, 45.94) * mm, v(-37.19, 43.54) * mm, v(-37.36, 41.05) * mm, v(-37.32, 38.6) * mm, v(-37.09, 36.69) * mm, v(-36.76, 35.32) * mm, v(-36.34, 34.06) * mm, v(-35.68, 32.66) * mm, v(-34.76, 31.22) * mm, v(-33.78, 29.95) * mm, v(-32.68, 28.98) * mm, v(-31.37, 28.43) * mm, v(-30.46, 28.22) * mm, v(-30, 28.11) * mm]});
            skFitSpline(sketch, "E110.0", {"points": [v(-29.92, 28.22) * mm, v(-30.14, 28.63) * mm, v(-30.58, 29.44) * mm, v(-31.2, 30.7) * mm, v(-31.69, 32.05) * mm, v(-32.04, 33.52) * mm, v(-32.31, 35.05) * mm, v(-32.56, 36.6) * mm, v(-32.83, 38.1) * mm, v(-33.02, 39.6) * mm, v(-33.08, 41.18) * mm, v(-32.92, 42.88) * mm, v(-32.6, 44.64) * mm, v(-32.18, 46.43) * mm, v(-31.7, 48.18) * mm, v(-31, 50.44) * mm, v(-30.46, 52.08) * mm, v(-30.08, 53.17) * mm]});
            skFitSpline(sketch, "E111.0", {"points": [v(-29.92, 28.22) * mm, v(-30.14, 28.63) * mm, v(-30.58, 29.44) * mm, v(-31.2, 30.7) * mm, v(-31.69, 32.05) * mm, v(-32.04, 33.52) * mm, v(-32.31, 35.05) * mm, v(-32.56, 36.6) * mm, v(-32.83, 38.1) * mm, v(-33.02, 39.6) * mm, v(-33.08, 41.18) * mm, v(-32.92, 42.88) * mm, v(-32.6, 44.64) * mm, v(-32.18, 46.43) * mm, v(-31.7, 48.18) * mm, v(-31, 50.44) * mm, v(-30.46, 52.08) * mm, v(-30.08, 53.17) * mm]});
            skLineSegment(sketch, "E112", {"start": v(-30, 28.11) * mm, "end": v(-29.98, 28.11) * mm});
            skLineSegment(sketch, "E113", {"start": v(-29.98, 28.11) * mm, "end": v(-29.92, 28.22) * mm});
            skLineSegment(sketch, "E114.trimOffspring", {"start": v(-21.23, 29.93) * mm, "end": v(-21.23, 22.4) * mm});
            skLineSegment(sketch, "E115.trimOffspring", {"start": v(-21.23, 45.77) * mm, "end": v(-21.23, 34.05) * mm});
            skLineSegment(sketch, "E116.trimOffspring", {"start": v(-33.16, 29.53) * mm, "end": v(-33.16, 22.02) * mm});
            skFitSpline(sketch, "E117.0", {"points": [v(-29.92, 28.22) * mm, v(-30.14, 28.63) * mm, v(-30.58, 29.44) * mm, v(-31.2, 30.7) * mm, v(-31.69, 32.05) * mm, v(-32.04, 33.52) * mm, v(-32.31, 35.05) * mm, v(-32.56, 36.6) * mm, v(-32.83, 38.1) * mm, v(-33.02, 39.6) * mm, v(-33.08, 41.18) * mm, v(-32.92, 42.88) * mm, v(-32.6, 44.64) * mm, v(-32.18, 46.43) * mm, v(-31.7, 48.18) * mm, v(-31, 50.44) * mm, v(-30.46, 52.08) * mm, v(-30.08, 53.17) * mm]});
            skLineSegment(sketch, "E118", {"start": v(-30.19, 53.27) * mm, "end": v(-30.1, 53.28) * mm});
            skLineSegment(sketch, "E119", {"start": v(-30.1, 53.28) * mm, "end": v(-30.08, 53.17) * mm});
            skLineSegment(sketch, "E120", {"start": v(-31.57, 31.79) * mm, "end": v(-31.57, 31.79) * mm});
            skLineSegment(sketch, "E121", {"start": v(-31.56, 31.75) * mm, "end": v(-31.57, 31.79) * mm});
            skLineSegment(sketch, "E122", {"start": v(-41.77, 34.55) * mm, "end": v(-41.77, 34.55) * mm});
            skLineSegment(sketch, "E123", {"start": v(-41.78, 34.55) * mm, "end": v(-41.76, 34.55) * mm});
            skLineSegment(sketch, "E124", {"start": v(-32.1, 47) * mm, "end": v(-32.01, 47) * mm});
            skLineSegment(sketch, "E125", {"start": v(-32.47, 45.53) * mm, "end": v(-32.39, 45.53) * mm});
            skFitSpline(sketch, "E126.trimOffspring", {"points": [v(-29.92, 28.22) * mm, v(-30.14, 28.63) * mm, v(-30.58, 29.44) * mm, v(-31.2, 30.7) * mm, v(-31.69, 32.05) * mm, v(-32.04, 33.52) * mm, v(-32.31, 35.05) * mm, v(-32.56, 36.6) * mm, v(-32.83, 38.1) * mm, v(-33.02, 39.6) * mm, v(-33.08, 41.18) * mm, v(-32.92, 42.88) * mm, v(-32.6, 44.64) * mm, v(-32.18, 46.43) * mm, v(-31.7, 48.18) * mm, v(-31, 50.44) * mm, v(-30.46, 52.08) * mm, v(-30.08, 53.17) * mm]});
            skFitSpline(sketch, "E127.trimOffspring", {"points": [v(-30.19, 53.27) * mm, v(-30.8, 52.98) * mm, v(-32.06, 52.4) * mm, v(-33.53, 51.55) * mm, v(-34.55, 50.7) * mm, v(-35.2, 49.94) * mm, v(-35.75, 49.07) * mm, v(-36.34, 47.77) * mm, v(-36.85, 45.94) * mm, v(-37.19, 43.54) * mm, v(-37.36, 41.05) * mm, v(-37.32, 38.6) * mm, v(-37.09, 36.69) * mm, v(-36.76, 35.32) * mm, v(-36.34, 34.06) * mm, v(-35.68, 32.66) * mm, v(-34.76, 31.22) * mm, v(-33.78, 29.95) * mm, v(-32.68, 28.98) * mm, v(-31.37, 28.43) * mm, v(-30.46, 28.22) * mm, v(-30, 28.11) * mm]});
            skLineSegment(sketch, "E128", {"start": v(-33.04, 42.3) * mm, "end": v(-32.97, 42.3) * mm});
            skLineSegment(sketch, "E129", {"start": v(-33.12, 40.39) * mm, "end": v(-33.04, 40.39) * mm});
            skFitSpline(sketch, "E130.trimOffspring", {"points": [v(-29.92, 28.22) * mm, v(-30.14, 28.63) * mm, v(-30.58, 29.44) * mm, v(-31.2, 30.7) * mm, v(-31.69, 32.05) * mm, v(-32.04, 33.52) * mm, v(-32.31, 35.05) * mm, v(-32.56, 36.6) * mm, v(-32.83, 38.1) * mm, v(-33.02, 39.6) * mm, v(-33.08, 41.18) * mm, v(-32.92, 42.88) * mm, v(-32.6, 44.64) * mm, v(-32.18, 46.43) * mm, v(-31.7, 48.18) * mm, v(-31, 50.44) * mm, v(-30.46, 52.08) * mm, v(-30.08, 53.17) * mm]});
            skPoint(sketch, "E131.1.internal.orphan", {"position": v(-32.85, 31.44) * mm});
            skPoint(sketch, "E132.2.internal.orphan", {"position": v(-32.1, 30.12) * mm});
            skPoint(sketch, "E133.1.internal.orphan", {"position": v(-34.74, 50.36) * mm});
            skPoint(sketch, "E134.end.orphan", {"position": v(-33.28, 50.36) * mm});
            skPoint(sketch, "E135.1.internal.orphan", {"position": v(-34.77, 48.88) * mm});
            skPoint(sketch, "E135.end.orphan", {"position": v(-33.6, 48.79) * mm});
            skFitSpline(sketch, "E136", {"points": [v(-35.82, 48.72) * mm, v(-35.3, 49.66) * mm, v(-34.74, 50.36) * mm], "startDerivative": vector(0.96, 1.89) * mm, "endDerivative": vector(1.2, 1.38) * mm});
            skFitSpline(sketch, "E137", {"points": [v(-35.9, 48.7) * mm, v(-35.57, 49.34) * mm, v(-35.36, 49.67) * mm, v(-35.03, 50.1) * mm, v(-34.84, 50.36) * mm], "startDerivative": vector(1.18, 2.26) * mm, "endDerivative": vector(0.85, 1.13) * mm});
            skFitSpline(sketch, "E138.trimOffspring", {"points": [v(-30, 28.19) * mm, v(-31.65, 31.78) * mm, v(-32.6, 36.37) * mm, v(-33.12, 41.13) * mm, v(-32, 47.3) * mm, v(-30.15, 53.2) * mm], "startDerivative": vector(-10.57, 19.5) * mm, "endDerivative": vector(8.94, 26.24) * mm});
            skLineSegment(sketch, "E139", {"start": v(-32.41, 35.2) * mm, "end": v(-32.32, 35.23) * mm});
            skSolve(sketch);
        }
        {
            var Q0;
            {var subQ4=sQuery(id+"F0.wireOp",EDGE,"E1");Q0=makeQuery(id+"F0.imprint","IMPRINT",FACE,{"disambiguationData":[TD([[makeQuery(id+"F0.imprint","IMPRINT",EDGE,{"derivedFrom":subQ4}),1.0]])]});}
            extrude(context, id + "F1", {"entities" : qUnion([Q0]), "depth" : 12.7 * mm, "offsetDistance" : 25.4 * mm});
        }
        {
            var Q0;
            Q0=makeQuery(id+"F0.imprint","IMPRINT",FACE,{"disambiguationData":[TD([[makeQuery(id+"F0.imprint","IMPRINT",EDGE,{"derivedFrom":sQuery(id+"F0.wireOp",EDGE,"E44")}),-1.0]])]});
            var Q1;
            {var subQ3=sQuery(id+"F0.wireOp",EDGE,"adc445e5-f0e8-431a-951c-fa998ec19b86.trimOffspring");Q1=makeQuery(id+"F0.imprint","IMPRINT",FACE,{"disambiguationData":[TD([[makeQuery(id+"F0.imprint","IMPRINT",EDGE,{"derivedFrom":subQ3}),1.0]])]});}
            var Q2;
            {var subQ10=sQuery(id+"F0.wireOp",EDGE,"E39");Q2=makeQuery(id+"F0.imprint","IMPRINT",FACE,{"disambiguationData":[TD([[makeQuery(id+"F0.imprint","IMPRINT",EDGE,{"derivedFrom":subQ10}),1.0]])]});}
            var Q3;
            Q3=makeQuery(id+"F0.imprint","IMPRINT",FACE,{"disambiguationData":[TD([[makeQuery(id+"F0.imprint","IMPRINT",EDGE,{"derivedFrom":sQuery(id+"F0.wireOp",EDGE,"E15")}),-1.0]])]});
            var Q4;
            Q4=makeQuery(id+"F0.imprint","IMPRINT",FACE,{"disambiguationData":[TD([[makeQuery(id+"F0.imprint","IMPRINT",EDGE,{"derivedFrom":sQuery(id+"F0.wireOp",EDGE,"E11")}),-1.0]])]});
            var Q5;
            {var subQ3=sQuery(id+"F0.wireOp",EDGE,"a4cc2007-8635-4577-b999-c099570f46cb.trimOffspring");Q5=makeQuery(id+"F0.imprint","IMPRINT",FACE,{"disambiguationData":[TD([[makeQuery(id+"F0.imprint","IMPRINT",EDGE,{"derivedFrom":subQ3}),1.0]])]});}
            var Q6;
            {var subQ3=sQuery(id+"F0.wireOp",EDGE,"eef5c619-cd36-4cef-b881-37f7d0e88043.trimOffspring");Q6=makeQuery(id+"F0.imprint","IMPRINT",FACE,{"disambiguationData":[TD([[makeQuery(id+"F0.imprint","IMPRINT",EDGE,{"derivedFrom":subQ3}),1.0]])]});}
            extrude(context, id + "F2", {"entities" : qUnion([Q0, Q1, Q2, Q3, Q4, Q5, Q6]), "operationType" : NewBodyOperationType.ADD, "depth" : 0.76 * mm, "offsetDistance" : 25.4 * mm});
        }
        {
            var Q0;
            {var subQ0=sQuery(id+"F0.wireOp",EDGE,"E24");Q0=makeQuery(id+"F0.imprint","IMPRINT",FACE,{"disambiguationData":[TD([[makeQuery(id+"F0.imprint","IMPRINT",EDGE,{"derivedFrom":subQ0}),-1.0]])]});}
            var Q1;
            {var subQ0=sQuery(id+"F0.wireOp",EDGE,"E28");Q1=makeQuery(id+"F0.imprint","IMPRINT",FACE,{"disambiguationData":[TD([[makeQuery(id+"F0.imprint","IMPRINT",EDGE,{"derivedFrom":subQ0}),1.0]])]});}
            var Q2;
            {var subQ0=sQuery(id+"F0.wireOp",EDGE,"E34");Q2=makeQuery(id+"F0.imprint","IMPRINT",FACE,{"disambiguationData":[TD([[makeQuery(id+"F0.imprint","IMPRINT",EDGE,{"derivedFrom":subQ0}),1.0]])]});}
            var Q3;
            Q3=makeQuery(id+"F2.opExtrude","CAP_FACE",FACE,{"disambiguationData":[OSD([sQuery(id+"F0.wireOp",EDGE,"E33"),sQuery(id+"F0.wireOp",EDGE,"E35"),sQuery(id+"F0.wireOp",EDGE,"E106.trimOffspring"),sQuery(id+"F0.wireOp",EDGE,"a4cc2007-8635-4577-b999-c099570f46cb.trimOffspring")])],"isStart":false});
            var Q4;
            {var subQ2=sQuery(id+"F0.wireOp",EDGE,"E131");Q4=makeQuery(id+"F0.imprint","IMPRINT",FACE,{"disambiguationData":[TD([[makeQuery(id+"F0.imprint","IMPRINT",EDGE,{"derivedFrom":subQ2}),1.0]])]});}
            var Q5;
            {var subQ0=sQuery(id+"F0.wireOp",EDGE,"E36");Q5=makeQuery(id+"F0.imprint","IMPRINT",FACE,{"disambiguationData":[TD([[makeQuery(id+"F0.imprint","IMPRINT",EDGE,{"derivedFrom":subQ0}),-1.0]])]});}
            var Q6;
            {var subQ0=sQuery(id+"F0.wireOp",EDGE,"E30");Q6=makeQuery(id+"F0.imprint","IMPRINT",FACE,{"disambiguationData":[TD([[makeQuery(id+"F0.imprint","IMPRINT",EDGE,{"derivedFrom":subQ0}),-1.0]])]});}
            var Q7;
            Q7=makeQuery(id+"F2.opExtrude","CAP_FACE",FACE,{"disambiguationData":[OSD([sQuery(id+"F0.wireOp",EDGE,"E21"),sQuery(id+"F0.wireOp",EDGE,"E23"),sQuery(id+"F0.wireOp",EDGE,"E106.trimOffspring"),sQuery(id+"F0.wireOp",EDGE,"adc445e5-f0e8-431a-951c-fa998ec19b86.trimOffspring")])],"isStart":false});
            var Q8;
            {var subQ0=sQuery(id+"F0.wireOp",EDGE,"E22");Q8=makeQuery(id+"F0.imprint","IMPRINT",FACE,{"disambiguationData":[TD([[makeQuery(id+"F0.imprint","IMPRINT",EDGE,{"derivedFrom":subQ0}),1.0]])]});}
            var Q9;
            {var subQ0=sQuery(id+"F0.wireOp",EDGE,"E135");Q9=makeQuery(id+"F0.imprint","IMPRINT",FACE,{"disambiguationData":[TD([[makeQuery(id+"F0.imprint","IMPRINT",EDGE,{"derivedFrom":subQ0}),1.0]])]});}
            var Q10;
            {var subQ0=sQuery(id+"F0.wireOp",EDGE,"170d1ef5-f9c9-48a6-807c-37094b8f979c");Q10=makeQuery(id+"F0.imprint","IMPRINT",FACE,{"disambiguationData":[TD([[makeQuery(id+"F0.imprint","IMPRINT",EDGE,{"derivedFrom":subQ0}),-1.0]])]});}
            var Q11;
            {var subQ3=sQuery(id+"F0.wireOp",EDGE,"adc445e5-f0e8-431a-951c-fa998ec19b86.trimOffspring");Q11=makeQuery(id+"F0.imprint","IMPRINT",FACE,{"disambiguationData":[TD([[makeQuery(id+"F0.imprint","IMPRINT",EDGE,{"derivedFrom":subQ3}),1.0]])]});}
            var Q12;
            {var subQ3=sQuery(id+"F0.wireOp",EDGE,"a4cc2007-8635-4577-b999-c099570f46cb.trimOffspring");Q12=makeQuery(id+"F0.imprint","IMPRINT",FACE,{"disambiguationData":[TD([[makeQuery(id+"F0.imprint","IMPRINT",EDGE,{"derivedFrom":subQ3}),1.0]])]});}
            extrude(context, id + "F3", {"entities" : qUnion([Q0, Q1, Q2, Q3, Q4, Q5, Q6, Q7, Q8, Q9, Q10, Q11, Q12]), "depth" : 7.62 * mm, "offsetDistance" : 25.4 * mm});
        }
    });
